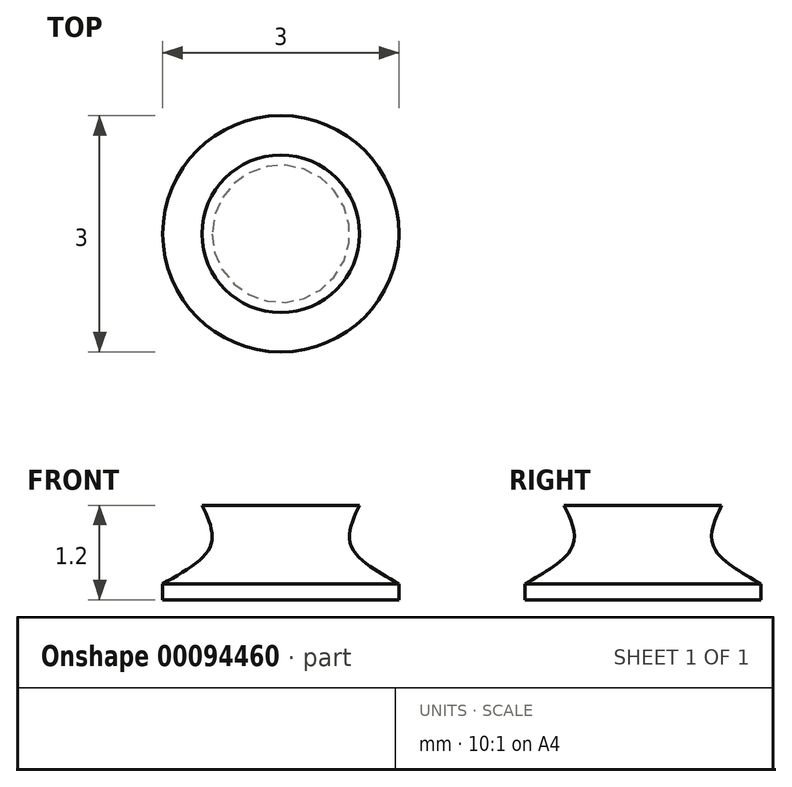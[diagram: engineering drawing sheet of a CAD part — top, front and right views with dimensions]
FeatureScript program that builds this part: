
annotation { "Feature Type Name" : "Feature", "Feature Type Description" : "" }
export const myFeature = defineFeature(function(context is Context, id is Id, definition is map)
    precondition{}
    {
        {
            var Q0;
            Q0=qCreatedBy(makeId("Front.planeOp"),FACE);
            var sketch = newSketch(context, id + "F0", { "sketchPlane" : qUnion([Q0])});
            skLineSegment(sketch, "E0", {"start": v(0, 1.2) * mm, "end": v(1, 1.2) * mm});
            skLineSegment(sketch, "E1", {"start": v(1.5, 0.2) * mm, "end": v(1.5, 0) * mm});
            skLineSegment(sketch, "E2", {"start": v(1.5, 0) * mm, "end": v(0, 0) * mm});
            skLineSegment(sketch, "E3", {"start": v(0, 0) * mm, "end": v(0, 1.2) * mm});
            skFitSpline(sketch, "E4", {"points": [v(1.5, 0.2) * mm, v(0.89, 0.7) * mm, v(1, 1.2) * mm], "startDerivative": vector(-1.45, 0.85) * mm, "endDerivative": vector(0.55, 1.16) * mm});
            skSolve(sketch);
        }
        {
            var Q0;
            Q0=makeQuery(id+"F0.imprint","IMPRINT",FACE,{"disambiguationData":[TD([[makeQuery(id+"F0.imprint","IMPRINT",EDGE,{"derivedFrom":sQuery(id+"F0.wireOp",EDGE,"E0")}),-1.0]])]});
            var Q1;
            Q1=sQuery(id+"F0.wireOp",EDGE,"E3");
            revolve(context, id + "F1", {"entities" : qUnion([Q0]), "axis" : qUnion([Q1]), "revolveType" : RevolveType.FULL});
        }
    });
